# Revit family: Strap_Tie-Simpson_Strong_Tie-MSTI-3D
name_source: partatom
category: Structural Connections
revit_build: Autodesk Revit Structure 2012 (Build: 20110309_2315(x64)
units: mm (PartAtom-declared; Revit-internal decimal feet)

## types (1)
- Strap_Tie-Simpson_Strong_Tie-MSTI-3D
    Code Reference = Use Type Catalog
    DF/SP_Allowable Loads_Tension_160 = Use Type Catalog
    Date Last Modified = April 18, 2013
    Default Elevation = 0"
    Description = Straps are designed to transfer tension loads in a wide variety of applications
    Equipment Abbreviation = Use Type Catalog
    Family Version = 1.0.0
    Fasteners_Quantity = 0
    Fasteners_Type = Use Type Catalog
    Is Void = Yes
    Length = 26"
    Manufacturer = Simpson Strong-Tie Company Inc.
    Metal Gauge = Use Type Catalog
    Model = Use Type Catalog
    Model Disclaimer = Contact Simpson Strong-Tie Company Inc. for more information
    Model ID = 42350A03-CBD9-4FC2-9489-3DC3EAF9B346
    Part Description = Straps are designed to transfer tension loads in a wide variety of applications
    Part Number = Use Type Catalog
    Product Documentation Link = http://www.strongtie.com
    Product Material = Steel - Simpson - Galvanized
    Provide Feedback = http://www.strongtie.com
    SPF/HF_Allowable Loads_Tension_160 = Use Type Catalog
    Type Comments = Strap Tie
    URL = http://www.strongtie.com
    Width = 2 1/16"

## geometry (parser evidence)
native form markers: Blend x1, Sweep x1
no freeform markers — native parametric forms only
